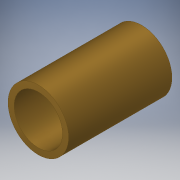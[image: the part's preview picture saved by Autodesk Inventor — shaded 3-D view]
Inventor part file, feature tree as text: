
AUTODESK INVENTOR PART (.ipt)
format: ipt  version: 2018 (Build 220112000, 112)  size: 98,304 bytes
history: native  units: in
note: dims shown in document units (in); Inventor stores cm internally (conversion verified against a paired STEP export)
features: extrude x1, sketch x1
ambient origin geometry x8: Origin, YZ Plane, XZ Plane, XY Plane, X Axis, Y Axis, Z Axis, Center Point
bodies: Solid1 (feature_tree)
feature tree (2):
  extrude  "Extrusion1"  Depth=0.533in
  sketch  "Sketch1"  dims[d0=0.312in d1=0.25in d2=0.533in d3=0.0in]
